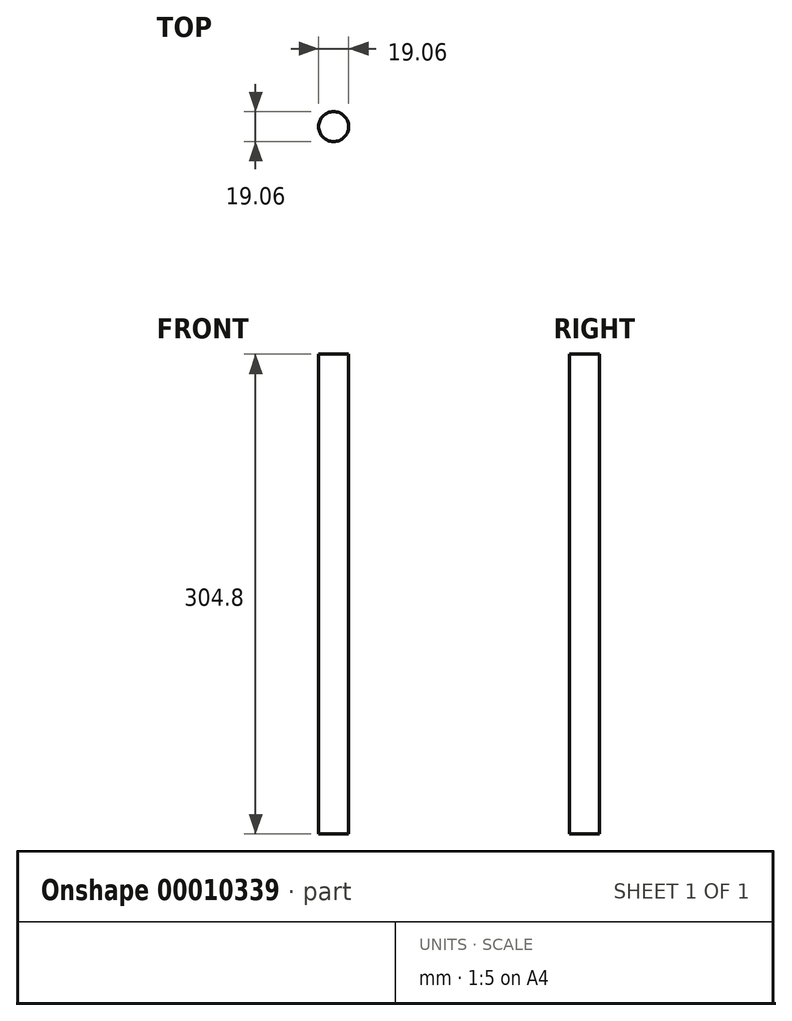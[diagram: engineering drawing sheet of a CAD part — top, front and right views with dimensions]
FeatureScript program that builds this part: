
annotation { "Feature Type Name" : "Feature", "Feature Type Description" : "" }
export const myFeature = defineFeature(function(context is Context, id is Id, definition is map)
    precondition{}
    {
        {
            var Q0;
            Q0=qCreatedBy(makeId("Top.planeOp"),FACE);
            var sketch = newSketch(context, id + "F0", { "sketchPlane" : qUnion([Q0])});
            skCircle(sketch, "E0", {"center": v(0, 0) * mm, "radius": 9.53 * mm});
            skSolve(sketch);
        }
        {
            var Q0;
            Q0 = qSketchRegion(id + "F0", true);
            extrude(context, id + "F1", {"entities" : qUnion([Q0]), "depth" : 304.8 * mm});
        }
    });
